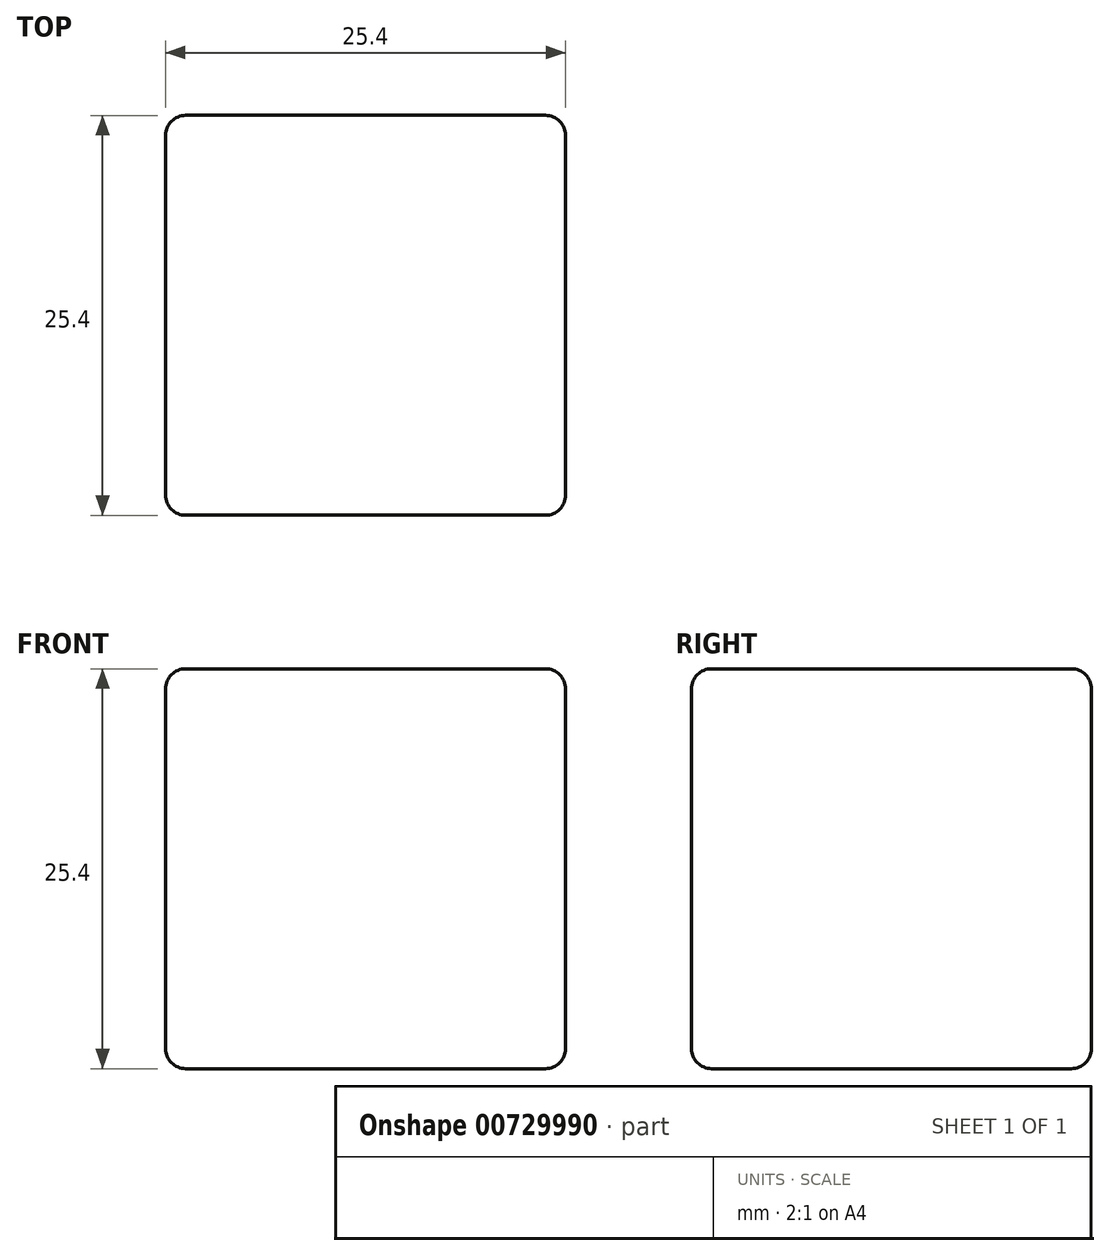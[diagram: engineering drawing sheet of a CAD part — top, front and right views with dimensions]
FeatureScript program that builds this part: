
annotation { "Feature Type Name" : "Feature", "Feature Type Description" : "" }
export const myFeature = defineFeature(function(context is Context, id is Id, definition is map)
    precondition{}
    {
        {
            var Q0;
            Q0=qCreatedBy(makeId("Top.planeOp"),FACE);
            var sketch = newSketch(context, id + "F0", { "sketchPlane" : qUnion([Q0])});
            skLineSegment(sketch, "E0.bottom", {"start": v(-18.4, -16.55) * mm, "end": v(7, -16.55) * mm});
            skLineSegment(sketch, "E0.top", {"start": v(-18.4, 8.85) * mm, "end": v(7, 8.85) * mm});
            skLineSegment(sketch, "E0.left", {"start": v(-18.4, -16.55) * mm, "end": v(-18.4, 8.85) * mm});
            skLineSegment(sketch, "E0.right", {"start": v(7, -16.55) * mm, "end": v(7, 8.85) * mm});
            skSolve(sketch);
        }
        {
            var Q0;
            Q0=makeQuery(id+"F0.imprint","IMPRINT",FACE,{"disambiguationData":[TD([[makeQuery(id+"F0.imprint","IMPRINT",EDGE,{"derivedFrom":sQuery(id+"F0.wireOp",EDGE,"E0.bottom")}),1.0]])]});
            extrude(context, id + "F1", {"entities" : qUnion([Q0]), "depth" : 25.4 * mm, "offsetDistance" : 25.4 * mm});
        }
        {
            var Q0;
            Q0=makeQuery(id+"F1.opExtrude","CAP_FACE",FACE,{"disambiguationData":[OSD([sQuery(id+"F0.wireOp",EDGE,"E0.bottom"),sQuery(id+"F0.wireOp",EDGE,"E0.top"),sQuery(id+"F0.wireOp",EDGE,"E0.left"),sQuery(id+"F0.wireOp",EDGE,"E0.right")])],"isStart":false});
            var Q1;
            Q1=makeQuery(id+"F1.opExtrude","SWEPT_FACE",FACE,{"disambiguationData":[OSD([sQuery(id+"F0.wireOp",EDGE,"E0.bottom")])]});
            var Q2;
            Q2=makeQuery(id+"F1.opExtrude","SWEPT_FACE",FACE,{"disambiguationData":[OSD([sQuery(id+"F0.wireOp",EDGE,"E0.right")])]});
            var Q3;
            Q3=makeQuery(id+"F1.opExtrude","SWEPT_FACE",FACE,{"disambiguationData":[OSD([sQuery(id+"F0.wireOp",EDGE,"E0.left")])]});
            var Q4;
            Q4=makeQuery(id+"F1.opExtrude","CAP_FACE",FACE,{"disambiguationData":[OSD([sQuery(id+"F0.wireOp",EDGE,"E0.bottom"),sQuery(id+"F0.wireOp",EDGE,"E0.top"),sQuery(id+"F0.wireOp",EDGE,"E0.left"),sQuery(id+"F0.wireOp",EDGE,"E0.right")])],"isStart":true});
            fillet(context, id + "F2", {"entities" : qUnion([Q0, Q1, Q2, Q3, Q4]), "radius" : 1.27 * mm, "tangentPropagation" : true, "allowEdgeOverflow" : false});
        }
    });
